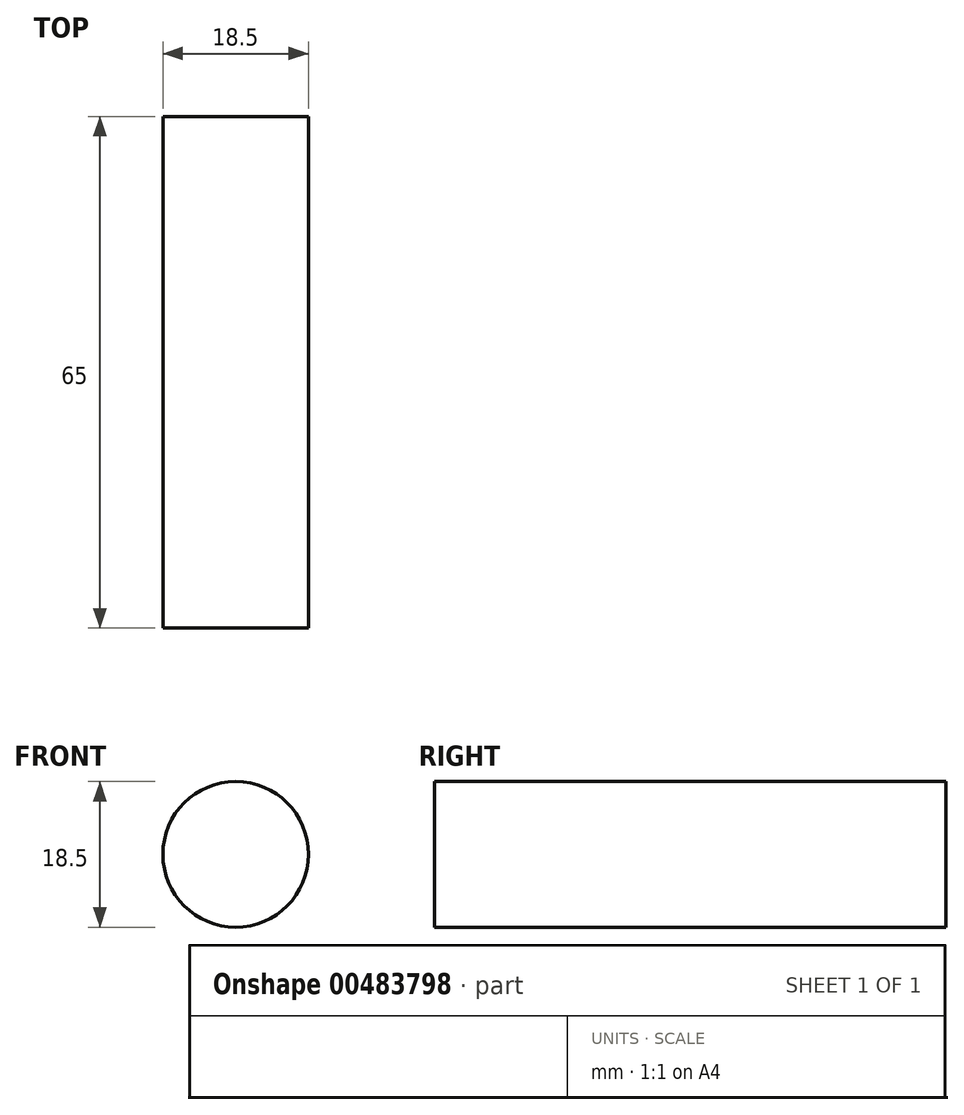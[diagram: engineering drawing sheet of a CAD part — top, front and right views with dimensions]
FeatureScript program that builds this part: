
annotation { "Feature Type Name" : "Feature", "Feature Type Description" : "" }
export const myFeature = defineFeature(function(context is Context, id is Id, definition is map)
    precondition{}
    {
        {
            var Q0;
            Q0=qCreatedBy(makeId("Front.planeOp"),FACE);
            var sketch = newSketch(context, id + "F0", { "sketchPlane" : qUnion([Q0])});
            skCircle(sketch, "E0", {"center": v(0, 0) * mm, "radius": 9.25 * mm});
            skSolve(sketch);
        }
        {
            var Q0;
            Q0=qSketchRegion(id+"F0",true);
            extrude(context, id + "F1", {"entities" : qUnion([Q0]), "depth" : 65 * mm});
        }
    });
